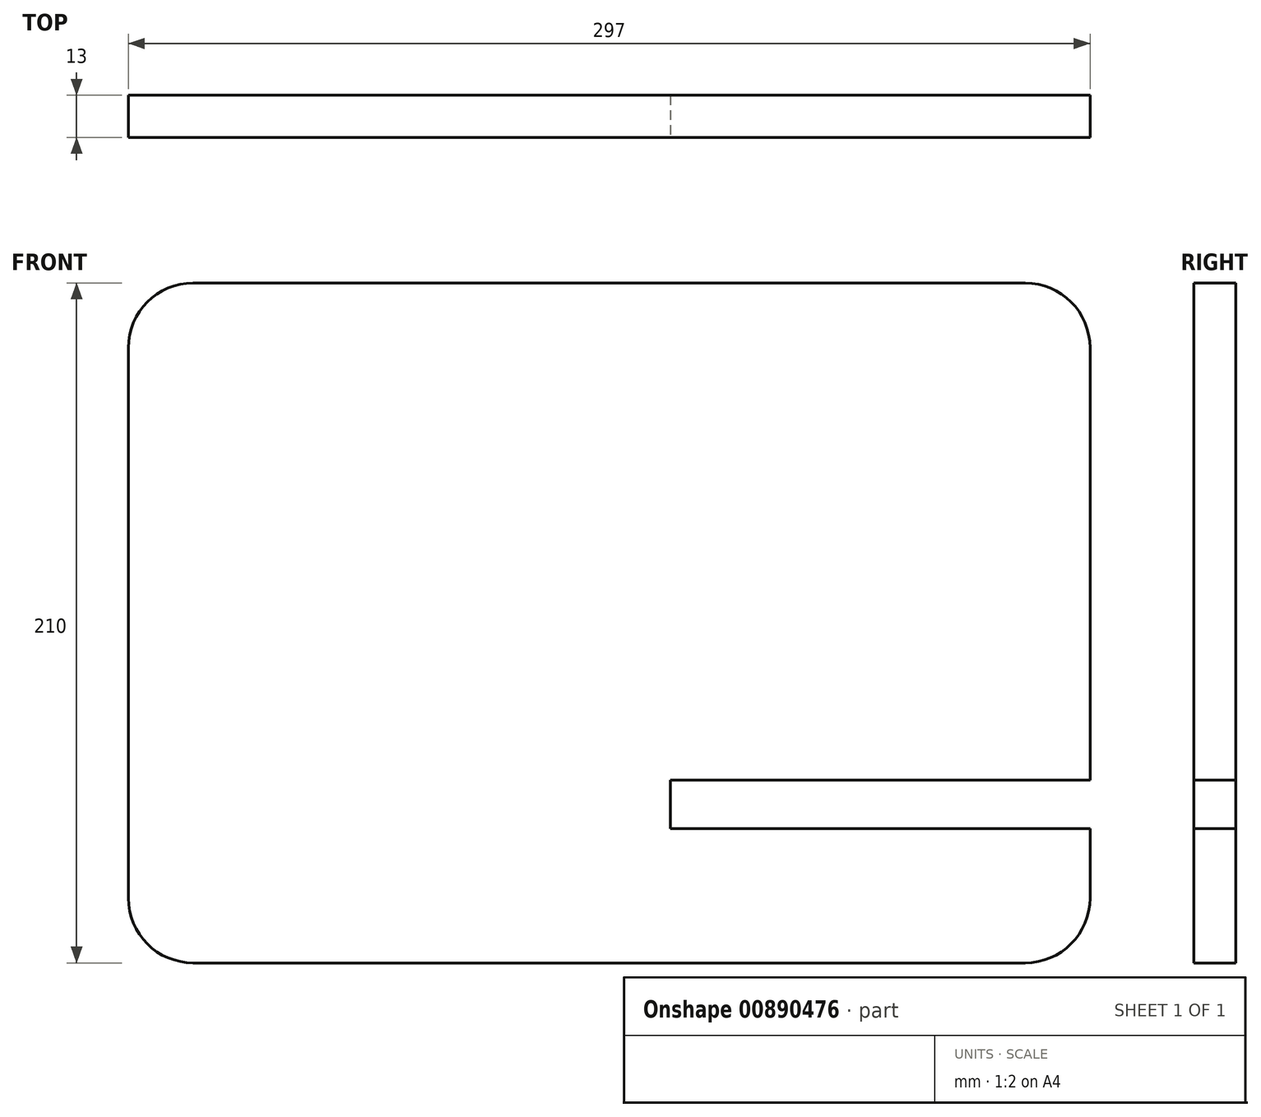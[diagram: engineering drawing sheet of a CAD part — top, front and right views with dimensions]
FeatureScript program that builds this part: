
annotation { "Feature Type Name" : "Feature", "Feature Type Description" : "" }
export const myFeature = defineFeature(function(context is Context, id is Id, definition is map)
    precondition{}
    {
        {
            var Q0;
            Q0=qCreatedBy(makeId("Front.planeOp"),FACE);
            var sketch = newSketch(context, id + "F0", { "sketchPlane" : qUnion([Q0])});
            skLineSegment(sketch, "E0.bottom", {"start": v(-48.8, 153.51) * mm, "end": v(208.2, 153.51) * mm});
            skLineSegment(sketch, "E0.top", {"start": v(-48.8, -56.49) * mm, "end": v(208.2, -56.49) * mm});
            skLineSegment(sketch, "E0.left", {"start": v(-68.8, 133.51) * mm, "end": v(-68.8, -36.49) * mm});
            skLineSegment(sketch, "E0.right", {"start": v(228.2, 133.51) * mm, "end": v(228.2, -36.49) * mm});
            skPoint(sketch, "E1.visualSharp", {"position": v(-68.8, 153.51) * mm});
            skArc(sketch, "E1.filletArc", {"start": v(-48.8, 153.51) * mm, "mid": v(-62.95, 147.66) * mm, "end": v(-68.8, 133.51) * mm});
            skPoint(sketch, "E2.visualSharp", {"position": v(228.2, 153.51) * mm});
            skArc(sketch, "E2.filletArc", {"start": v(228.2, 133.51) * mm, "mid": v(222.34, 147.66) * mm, "end": v(208.2, 153.51) * mm});
            skPoint(sketch, "E3.visualSharp", {"position": v(-68.8, -56.49) * mm});
            skArc(sketch, "E3.filletArc", {"start": v(-68.8, -36.49) * mm, "mid": v(-62.95, -50.63) * mm, "end": v(-48.8, -56.49) * mm});
            skPoint(sketch, "E4.visualSharp", {"position": v(228.2, -56.49) * mm});
            skArc(sketch, "E4.filletArc", {"start": v(208.2, -56.49) * mm, "mid": v(222.34, -50.63) * mm, "end": v(228.2, -36.49) * mm});
            skSolve(sketch);
        }
        {
            var Q0;
            Q0 = qSketchRegion(id + "F0", true);
            extrude(context, id + "F1", {"entities" : qUnion([Q0]), "depth" : 13 * mm, "offsetDistance" : 25 * mm});
        }
        {
            var Q0;
            Q0=makeQuery(id+"F1.opExtrude","CAP_FACE",FACE,{"disambiguationData":[OSD([sQuery(id+"F0.wireOp",EDGE,"E0.bottom"),sQuery(id+"F0.wireOp",EDGE,"E0.top"),sQuery(id+"F0.wireOp",EDGE,"E0.left"),sQuery(id+"F0.wireOp",EDGE,"E0.right"),sQuery(id+"F0.wireOp",EDGE,"E1.filletArc"),sQuery(id+"F0.wireOp",EDGE,"E2.filletArc"),sQuery(id+"F0.wireOp",EDGE,"E3.filletArc"),sQuery(id+"F0.wireOp",EDGE,"E4.filletArc")])],"isStart":false});
            var sketch = newSketch(context, id + "F2", { "sketchPlane" : qUnion([Q0])});
            skLineSegment(sketch, "E5.bottom", {"start": v(228.56, 0) * mm, "end": v(98.56, 0) * mm});
            skLineSegment(sketch, "E5.top", {"start": v(228.56, -15) * mm, "end": v(98.56, -15) * mm});
            skLineSegment(sketch, "E5.left", {"start": v(228.56, 0) * mm, "end": v(228.56, -15) * mm});
            skLineSegment(sketch, "E5.right", {"start": v(98.56, 0) * mm, "end": v(98.56, -15) * mm});
            skSolve(sketch);
        }
        {
            var Q0;
            Q0 = qSketchRegion(id + "F2", true);
            extrude(context, id + "F3", {"entities" : qUnion([Q0]), "operationType" : NewBodyOperationType.REMOVE, "oppositeDirection" : true, "depth" : 25 * mm, "offsetDistance" : 25 * mm});
        }
    });
